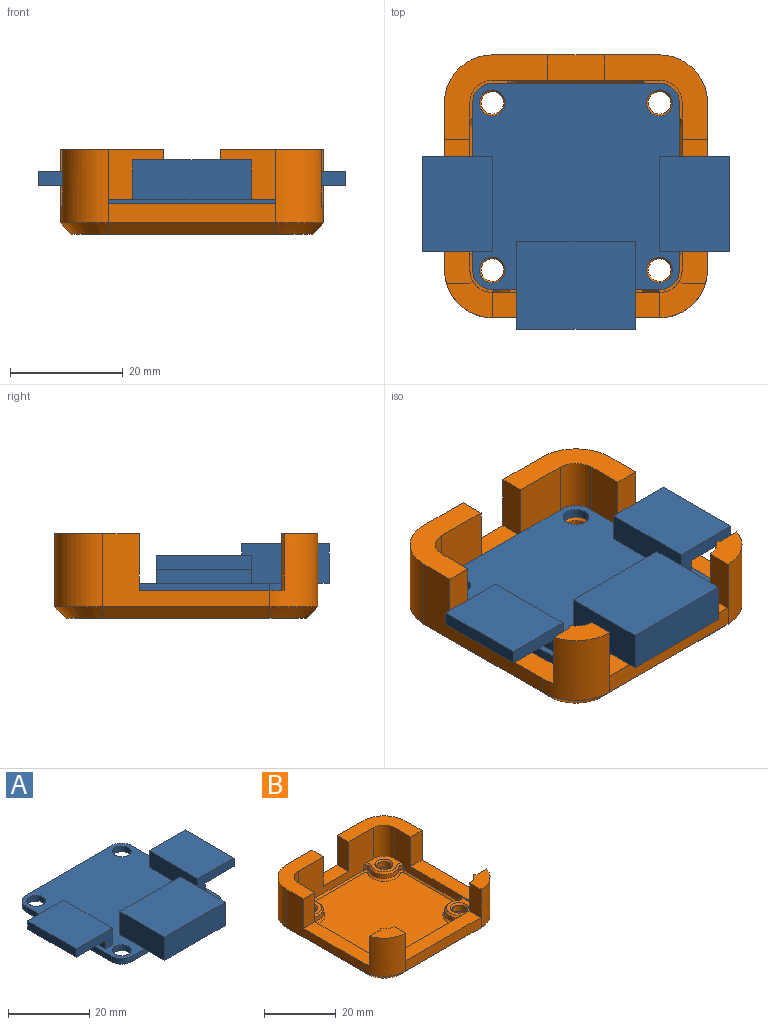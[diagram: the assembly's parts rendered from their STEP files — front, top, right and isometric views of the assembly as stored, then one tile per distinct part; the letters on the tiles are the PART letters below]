
ASSEMBLY  parts=2 mates=1
PART A: 34 faces, bbox 54.7x43.7x8.7 mm
  f0: plane 36.7x36.7mm, normal (0,0,1), area 1006.6mm2, adj f1,f2,f3,f4,f5,f6,f7,f8
  f1: plane 29.7x1.7mm, normal (0,-1,0), area 50.5mm2, adj f0,f2,f12,f13,f24
  f2: cylinder r=3.5mm len=3.5mm, axis (0,0,-1), area 9.3mm2, adj f0,f1,f3,f13
  f3: plane 29.7x1.7mm, normal (1,0,0), area 50.5mm2, adj f0,f2,f4,f13
  f4: cylinder r=3.5mm len=3.5mm, axis (0,0,-1), area 9.3mm2, adj f0,f3,f5,f13
  f5: plane 29.7x1.7mm, normal (0,1,0), area 50.5mm2, adj f0,f4,f6,f13
  f6: cylinder r=3.5mm len=3.5mm, axis (0,0,-1), area 9.3mm2, adj f0,f5,f7,f13
  f7: plane 29.7x1.7mm, normal (-1,0,0), area 50.5mm2, adj f0,f6,f12,f13
  f8: cylinder r=2.3mm len=4.6mm, axis (0,0,-1), area 24.6mm2, adj f0,f13
  f9: cylinder r=2.3mm len=4.6mm, axis (0,0,-1), area 24.6mm2, adj f0,f13
  f10: cylinder r=2.3mm len=4.6mm, axis (0,0,-1), area 24.6mm2, adj f0,f13
  f11: cylinder r=2.3mm len=4.6mm, axis (0,0,-1), area 24.6mm2, adj f0,f13
  f12: cylinder r=3.5mm len=3.5mm, axis (0,0,-1), area 9.3mm2, adj f0,f1,f7,f13
  f13: plane 36.7x36.7mm, normal (0,0,-1), area 1269.9mm2, adj f1,f2,f3,f4,f5,f6,f7,f8
  f14: plane 12.5x5mm, normal (0,1,0), area 37.5mm2, adj f0,f15,f17,f18,f32,f33
  f15: plane 16.95x2.5mm, normal (-1,0,0), area 42.4mm2, adj f0,f14,f16,f32
  f16: plane 12.5x5mm, normal (0,-1,0), area 37.5mm2, adj f0,f15,f17,f18,f32,f33
  f17: plane 16.95x5mm, normal (1,0,0), area 84.8mm2, adj f0,f14,f16,f18
  f18: plane 16.95x12.5mm, normal (0,0,1), area 211.9mm2, adj f14,f16,f17,f33
  f19: plane 12.5x5mm, normal (0,1,0), area 37.5mm2, adj f0,f20,f22,f23,f30,f31
  f20: plane 16.95x5mm, normal (-1,0,0), area 84.8mm2, adj f0,f19,f21,f23
  f21: plane 12.5x5mm, normal (0,-1,0), area 37.5mm2, adj f0,f20,f22,f23,f30,f31
  f22: plane 16.95x2.5mm, normal (1,0,0), area 42.4mm2, adj f0,f19,f21,f30
  f23: plane 16.95x12.5mm, normal (0,0,1), area 211.9mm2, adj f19,f20,f21,f31
  f24: plane 21x7mm, normal (0,0,-1), area 147mm2, adj f1,f26,f27,f28
  f25: plane 21x7mm, normal (0,1,0), area 147mm2, adj f0,f26,f28,f29
  f26: plane 15.5x7mm, normal (-1,0,0), area 108.5mm2, adj f0,f24,f25,f27,f29
  f27: plane 21x7mm, normal (0,-1,0), area 147mm2, adj f24,f26,f28,f29
  f28: plane 15.5x7mm, normal (1,0,0), area 108.5mm2, adj f0,f24,f25,f27,f29
  f29: plane 21x15.5mm, normal (0,0,1), area 325.5mm2, adj f25,f26,f27,f28
  f30: plane 16.95x10mm, normal (0,0,-1), area 169.5mm2, adj f19,f21,f22,f31
  f31: plane 16.95x2.5mm, normal (1,0,0), area 42.4mm2, adj f19,f21,f23,f30
  f32: plane 16.95x10mm, normal (0,0,-1), area 169.5mm2, adj f14,f15,f16,f33
  f33: plane 16.95x2.5mm, normal (-1,0,0), area 42.4mm2, adj f14,f16,f18,f32
PART B: 97 faces, bbox 46.7x46.7x15 mm
  f0: plane 37.2x36.7mm, normal (0,0,1), area 1126.7mm2, adj f52,f53,f54,f55,f56,f57,f58,f59
  f1: plane 9.5x4.5mm, normal (1,0,0), area 42.7mm2, adj f8,f21,f37,f82
  f2: plane 9.5x4.5mm, normal (-1,0,0), area 42.7mm2, adj f10,f25,f28,f82
  f3: plane 29.7x12.5mm, normal (0,-1,0), area 255.5mm2, adj f5,f22,f23,f30,f31,f33,f34,f39
  f4: plane 29.7x12.5mm, normal (1,0,0), area 123.5mm2, adj f7,f21,f22,f32,f34,f39,f45,f46
  f5: plane 10x4.5mm, normal (0,0,1), area 45mm2, adj f3,f13,f30,f33
  f6: plane 25.7x5.02mm, normal (0,0,1), area 115.8mm2, adj f10,f11,f24,f25,f26,f27,f29
  f7: plane 25.7x5.02mm, normal (0,0,1), area 115.8mm2, adj f4,f8,f19,f21,f32,f35,f36
  f8: cylinder r=8.5mm len=13mm, axis (0,0,1), area 148.2mm2, adj f1,f7,f9,f19,f36,f37,f92
  f9: plane 29.7x3.5mm, normal (0,-1,0), area 104mm2, adj f8,f10,f82,f91
  f10: cylinder r=8.5mm len=13mm, axis (0,0,1), area 148.2mm2, adj f2,f6,f9,f11,f26,f28,f89
  f11: plane 29.7x13mm, normal (1,0,0), area 154.1mm2, adj f6,f10,f12,f29,f31,f87
  f12: cylinder r=8.5mm len=13mm, axis (0,0,1), area 173.6mm2, adj f11,f13,f31,f85
  f13: plane 29.7x13mm, normal (0,1,0), area 286.1mm2, adj f5,f12,f14,f30,f31,f33,f34,f86
  f14: cylinder r=8.5mm len=13mm, axis (0,0,1), area 173.6mm2, adj f13,f19,f34,f88
  f15: cylinder r=2mm len=4mm, axis (0,0,1), area 25.1mm2, adj f77,f93
  f16: cylinder r=2mm len=4mm, axis (0,0,1), area 25.1mm2, adj f78,f94
  f17: cylinder r=2mm len=4mm, axis (0,0,1), area 25.1mm2, adj f79,f95
  f18: cylinder r=2mm len=4mm, axis (0,0,1), area 25.1mm2, adj f80,f96
  f19: plane 29.7x13mm, normal (-1,0,0), area 154.1mm2, adj f7,f8,f14,f32,f34,f90
  f20: plane 42.7x42.7mm, normal (0,0,-1), area 1586mm2, adj f85,f86,f87,f88,f89,f90,f91,f92
  f21: cylinder r=4mm len=10.59mm, axis (0,0,-1), area 45.3mm2, adj f1,f4,f7,f35,f37,f45,f73,f81
  f22: cylinder r=4mm len=10.5mm, axis (0,0,-1), area 66mm2, adj f3,f4,f34,f39
  f23: cylinder r=4mm len=10.5mm, axis (0,0,-1), area 66mm2, adj f3,f24,f31,f41
  f24: plane 29.7x12.5mm, normal (-1,0,0), area 123.5mm2, adj f6,f23,f25,f29,f31,f41,f43,f47
  f25: cylinder r=4mm len=10.59mm, axis (0,0,-1), area 45.3mm2, adj f2,f6,f24,f27,f28,f43,f65,f81
  f26: plane 10x4.12mm, normal (0,1,0), area 41.2mm2, adj f6,f10,f27,f28
  f27: plane 10x0.52mm, normal (0.71,0.71,0), area 7.4mm2, adj f6,f25,f26,f28
  f28: plane 8.12x6.52mm, normal (0,0,1), area 32.8mm2, adj f2,f10,f25,f26,f27
  f29: plane 10x4.5mm, normal (0,-1,0), area 45mm2, adj f6,f11,f24,f31
  f30: plane 10x4.5mm, normal (-1,0,0), area 45mm2, adj f3,f5,f13,f31
  f31: plane 18.35x15mm, normal (0,0,1), area 117.8mm2, adj f3,f11,f12,f13,f23,f24,f29,f30
  f32: plane 10x4.5mm, normal (0,-1,0), area 45mm2, adj f4,f7,f19,f34
  f33: plane 10x4.5mm, normal (1,0,0), area 45mm2, adj f3,f5,f13,f34
  f34: plane 18.35x15mm, normal (0,0,1), area 117.8mm2, adj f3,f4,f13,f14,f19,f22,f32,f33
  f35: plane 10x0.52mm, normal (-0.71,0.71,0), area 7.4mm2, adj f7,f21,f36,f37
  f36: plane 10x4.12mm, normal (0,1,0), area 41.2mm2, adj f7,f8,f35,f37
  f37: plane 8.12x6.52mm, normal (0,0,1), area 32.8mm2, adj f1,f8,f21,f35,f36
  f38: cylinder r=4.1mm len=6.51mm, axis (0,0,-1), area 17.4mm2, adj f50,f51,f60,f69
  f39: plane 7.6x7.6mm, normal (0,0,1), area 27.7mm2, adj f3,f4,f22,f68,f69,f70,f79
  f40: cylinder r=4.1mm len=6.51mm, axis (0,0,-1), area 17.4mm2, adj f48,f49,f56,f75
  f41: plane 7.6x7.6mm, normal (0,0,1), area 27.7mm2, adj f3,f23,f24,f74,f75,f76,f77
  f42: cylinder r=4.1mm len=7.13mm, axis (0,0,-1), area 18.7mm2, adj f47,f52,f66,f83
  f43: plane 7.6x7.6mm, normal (0,0,1), area 25.6mm2, adj f24,f25,f65,f66,f67,f78
  f44: cylinder r=4.1mm len=7.13mm, axis (0,0,-1), area 18.7mm2, adj f46,f64,f72,f84
  f45: plane 7.6x7.6mm, normal (0,0,1), area 25.6mm2, adj f4,f21,f71,f72,f73,f80
  f46: cylinder r=1mm len=1.59mm, axis (0,0,-1), area 3.3mm2, adj f4,f44,f63,f71
  f47: cylinder r=1mm len=1.59mm, axis (0,0,-1), area 3.3mm2, adj f24,f42,f53,f67
  f48: cylinder r=1mm len=1.59mm, axis (0,0,-1), area 3.3mm2, adj f3,f40,f57,f76
  f49: cylinder r=1mm len=1.59mm, axis (0,0,-1), area 3.3mm2, adj f24,f40,f55,f74
  f50: cylinder r=1mm len=1.59mm, axis (0,0,-1), area 3.3mm2, adj f3,f38,f59,f68
  f51: cylinder r=1mm len=1.59mm, axis (0,0,-1), area 3.3mm2, adj f4,f38,f61,f70
  f52: cone r=4.1mm half-angle=45deg, axis (0,0,-1), area 9.4mm2, adj f0,f42,f53,f83
  f53: cone r=0.5mm half-angle=45deg, axis (0,0,1), area 1.2mm2, adj f0,f47,f52,f54
  f54: plane 21.45x0.5mm, normal (-0.71,0,0.71), area 15.2mm2, adj f0,f24,f53,f55
  f55: cone r=0.5mm half-angle=45deg, axis (0,0,1), area 1.2mm2, adj f0,f49,f54,f56
  f56: cone r=4.1mm half-angle=45deg, axis (0,0,-1), area 8.7mm2, adj f0,f40,f55,f57
  f57: cone r=0.5mm half-angle=45deg, axis (0,0,1), area 1.2mm2, adj f0,f48,f56,f58
  f58: plane 21.45x0.5mm, normal (0,-0.71,0.71), area 15.2mm2, adj f0,f3,f57,f59
  f59: cone r=0.5mm half-angle=45deg, axis (0,0,1), area 1.2mm2, adj f0,f50,f58,f60
  f60: cone r=4.1mm half-angle=45deg, axis (0,0,-1), area 8.7mm2, adj f0,f38,f59,f61
  f61: cone r=0.5mm half-angle=45deg, axis (0,0,1), area 1.2mm2, adj f0,f51,f60,f62
  f62: plane 21.45x0.5mm, normal (0.71,0,0.71), area 15.2mm2, adj f0,f4,f61,f63
  f63: cone r=0.5mm half-angle=45deg, axis (0,0,1), area 1.2mm2, adj f0,f46,f62,f64
  f64: cone r=4.1mm half-angle=45deg, axis (0,0,-1), area 9.4mm2, adj f0,f44,f63,f84
  f65: cone r=1.5mm half-angle=45deg, axis (0,0,1), area 0.4mm2, adj f25,f43,f66,f81
  f66: cone r=3.6mm half-angle=45deg, axis (0,0,-1), area 11mm2, adj f42,f43,f65,f67,f81,f83
  f67: cone r=1.5mm half-angle=45deg, axis (0,0,1), area 1.4mm2, adj f24,f43,f47,f66
  f68: cone r=1.5mm half-angle=45deg, axis (0,0,1), area 1.4mm2, adj f3,f39,f50,f69
  f69: cone r=3.6mm half-angle=45deg, axis (0,0,-1), area 7.7mm2, adj f38,f39,f68,f70
  f70: cone r=1.5mm half-angle=45deg, axis (0,0,1), area 1.4mm2, adj f4,f39,f51,f69
  f71: cone r=1.5mm half-angle=45deg, axis (0,0,1), area 1.4mm2, adj f4,f45,f46,f72
  f72: cone r=3.6mm half-angle=45deg, axis (0,0,-1), area 11mm2, adj f44,f45,f71,f73,f81,f84
  f73: cone r=1.5mm half-angle=45deg, axis (0,0,1), area 0.4mm2, adj f21,f45,f72,f81
  f74: cone r=1.5mm half-angle=45deg, axis (0,0,1), area 1.4mm2, adj f24,f41,f49,f75
  f75: cone r=3.6mm half-angle=45deg, axis (0,0,-1), area 7.7mm2, adj f40,f41,f74,f76
  f76: cone r=1.5mm half-angle=45deg, axis (0,0,1), area 1.4mm2, adj f3,f41,f48,f75
  f77: cone r=2mm half-angle=45deg, axis (0,0,1), area 10mm2, adj f15,f41
  f78: cone r=2mm half-angle=45deg, axis (0,0,1), area 10mm2, adj f16,f43
  f79: cone r=2mm half-angle=45deg, axis (0,0,1), area 10mm2, adj f17,f39
  f80: cone r=2mm half-angle=45deg, axis (0,0,1), area 10mm2, adj f18,f45
  f81: plane 29.7x3.5mm, normal (0,1,0), area 93mm2, adj f0,f21,f25,f65,f66,f72,f73,f82
  f82: plane 29.7x4.5mm, normal (0,0,1), area 133.6mm2, adj f1,f2,f9,f81
  f83: plane 2.04x1mm, normal (-0.93,0.36,0), area 1.4mm2, adj f0,f42,f52,f66,f81
  f84: plane 2.04x1mm, normal (0.93,0.36,0), area 1.4mm2, adj f0,f44,f64,f72,f81
  f85: cone r=8.5mm half-angle=45deg, axis (0,0,1), area 33.3mm2, adj f12,f20,f86,f87
  f86: plane 29.7x2mm, normal (0,0.71,-0.71), area 84mm2, adj f13,f20,f85,f88
  f87: plane 29.7x2mm, normal (0.71,0,-0.71), area 84mm2, adj f11,f20,f85,f89
  f88: cone r=8.5mm half-angle=45deg, axis (0,0,1), area 33.3mm2, adj f14,f20,f86,f90
  f89: cone r=8.5mm half-angle=45deg, axis (0,0,1), area 33.3mm2, adj f10,f20,f87,f91
  f90: plane 29.7x2mm, normal (-0.71,0,-0.71), area 84mm2, adj f19,f20,f88,f92
  f91: plane 29.7x2mm, normal (0,-0.71,-0.71), area 84mm2, adj f9,f20,f89,f92
  f92: cone r=8.5mm half-angle=45deg, axis (0,0,1), area 33.3mm2, adj f8,f20,f90,f91
  f93: cone r=4mm half-angle=45deg, axis (0,0,-1), area 53.3mm2, adj f15,f20
  f94: cone r=4mm half-angle=45deg, axis (0,0,-1), area 53.3mm2, adj f16,f20
  f95: cone r=4mm half-angle=45deg, axis (0,0,-1), area 53.3mm2, adj f17,f20
  f96: cone r=4mm half-angle=45deg, axis (0,0,-1), area 53.3mm2, adj f18,f20
PLACE A t=(-0.17,-0.17,1.68)mm
PLACE B t=(-0.17,-0.17,-0.82)mm
MATE fastened A.f6 <-> B.f14  axis (0,0,-1) through (-15.02,14.68,1.68)mm
